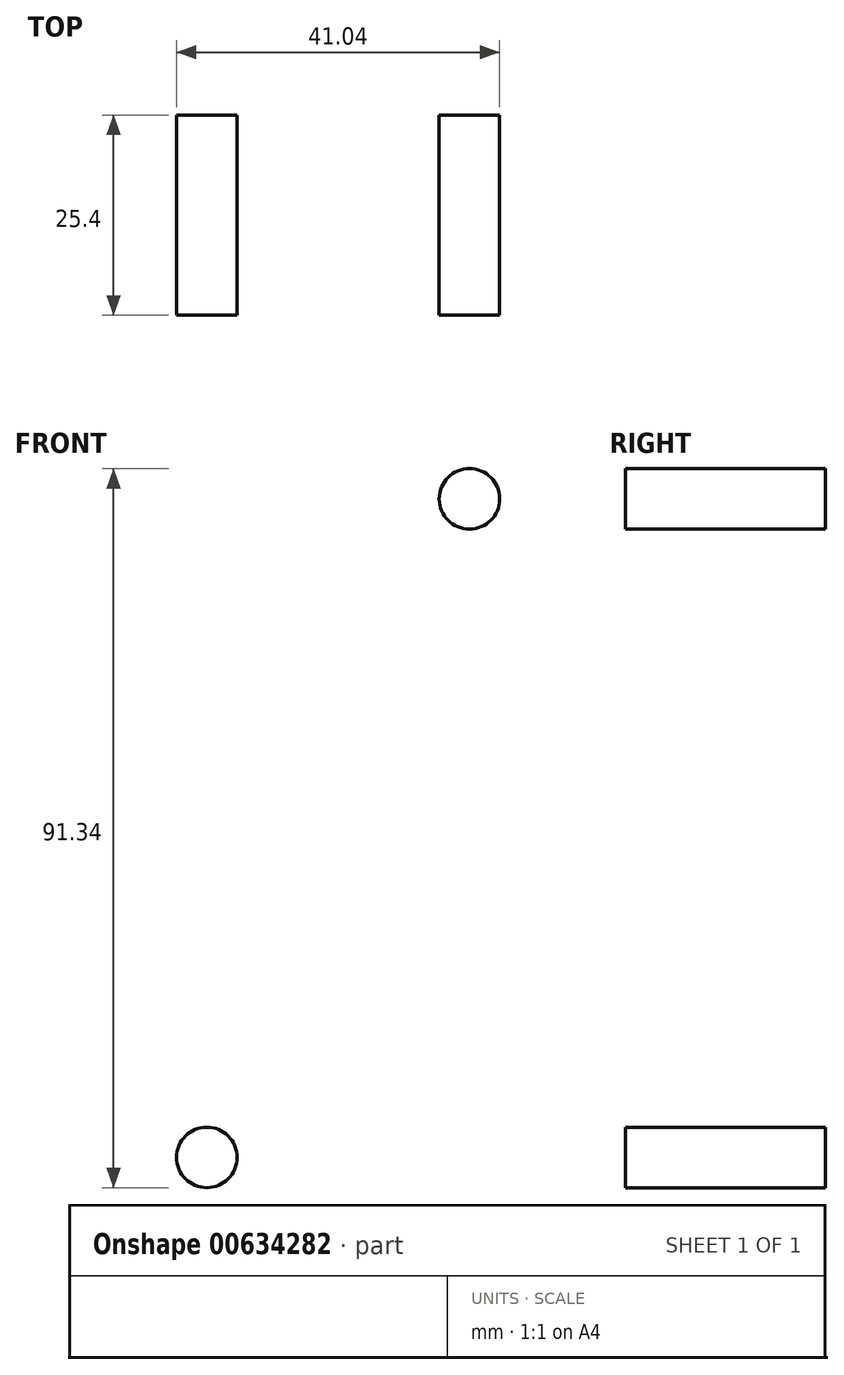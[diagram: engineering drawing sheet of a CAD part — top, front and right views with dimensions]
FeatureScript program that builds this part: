
annotation { "Feature Type Name" : "Feature", "Feature Type Description" : "" }
export const myFeature = defineFeature(function(context is Context, id is Id, definition is map)
    precondition{}
    {
        {
            var Q0;
            Q0=qCreatedBy(makeId("Front.planeOp"),FACE);
            var sketch = newSketch(context, id + "F0", { "sketchPlane" : qUnion([Q0])});
            skLineSegment(sketch, "E0.bottom", {"start": v(25.4, -50.8) * mm, "end": v(-25.4, -50.8) * mm});
            skLineSegment(sketch, "E0.top", {"start": v(25.4, 50.8) * mm, "end": v(-25.4, 50.8) * mm});
            skLineSegment(sketch, "E0.left", {"start": v(25.4, -50.8) * mm, "end": v(25.4, 50.8) * mm});
            skLineSegment(sketch, "E0.right", {"start": v(-25.4, -50.8) * mm, "end": v(-25.4, 50.8) * mm});
            skPoint(sketch, "E0.middle", {"position": v(0, 0) * mm});
            skCircle(sketch, "E1", {"center": v(0, -27.91) * mm, "radius": 7.62 * mm});
            skCircle(sketch, "E2.MirrorC", {"center": v(0, 27.91) * mm, "radius": 7.62 * mm});
            skSolve(sketch);
        }
        {
            var Q0;
            Q0=makeQuery(id+"F0.imprint","IMPRINT",FACE,{"disambiguationData":[TD([[makeQuery(id+"F0.imprint","IMPRINT",EDGE,{"derivedFrom":sQuery(id+"F0.wireOp",EDGE,"E0.bottom")}),-1.0]])]});
            extrude(context, id + "F1", {"entities" : qUnion([Q0]), "endBound" : BoundingType.SYMMETRIC, "depth" : 25.4 * mm, "offsetDistance" : 25.4 * mm});
        }
        {
            var Q0;
            Q0=makeQuery(id+"F1.opExtrude","SWEPT_EDGE",EDGE,{"disambiguationData":[OSD([sQuery(id+"F0.wireOp",EDGE,"E0.top"),sQuery(id+"F0.wireOp",EDGE,"E0.left")])]});
            var Q1;
            Q1=makeQuery(id+"F1.opExtrude","SWEPT_EDGE",EDGE,{"disambiguationData":[OSD([sQuery(id+"F0.wireOp",EDGE,"E0.bottom"),sQuery(id+"F0.wireOp",EDGE,"E0.left")])]});
            var Q2;
            Q2=makeQuery(id+"F1.opExtrude","SWEPT_EDGE",EDGE,{"disambiguationData":[OSD([sQuery(id+"F0.wireOp",EDGE,"E0.bottom"),sQuery(id+"F0.wireOp",EDGE,"E0.right")])]});
            var Q3;
            Q3=makeQuery(id+"F1.opExtrude","SWEPT_EDGE",EDGE,{"disambiguationData":[OSD([sQuery(id+"F0.wireOp",EDGE,"E0.top"),sQuery(id+"F0.wireOp",EDGE,"E0.right")])]});
            fillet(context, id + "F2", {"entities" : qUnion([Q0, Q1, Q2, Q3]), "radius" : 5.08 * mm, "tangentPropagation" : true, "allowEdgeOverflow" : false});
        }
        {
            var Q0;
            Q0=makeQuery(id+"F1.opExtrude","CAP_FACE",FACE,{"disambiguationData":[OSD([sQuery(id+"F0.wireOp",EDGE,"E0.bottom"),sQuery(id+"F0.wireOp",EDGE,"E0.top"),sQuery(id+"F0.wireOp",EDGE,"E0.left"),sQuery(id+"F0.wireOp",EDGE,"E0.right"),sQuery(id+"F0.wireOp",EDGE,"E1"),sQuery(id+"F0.wireOp",EDGE,"E2.MirrorC")])],"isStart":false});
            var sketch = newSketch(context, id + "F3", { "sketchPlane" : qUnion([Q0])});
            skCircle(sketch, "E3", {"center": v(-16.68, 41.83) * mm, "radius": 3.84 * mm});
            skCircle(sketch, "E4.MirrorC", {"center": v(16.68, 41.83) * mm, "radius": 3.84 * mm});
            skCircle(sketch, "E5.MirrorC", {"center": v(-16.68, -41.83) * mm, "radius": 3.84 * mm});
            skCircle(sketch, "E6.MirrorC", {"center": v(16.68, -41.83) * mm, "radius": 3.84 * mm});
            skSolve(sketch);
        }
        {
            var Q0;
            Q0=makeQuery(id+"F3.imprint","IMPRINT",FACE,{"disambiguationData":[TD([[makeQuery(id+"F3.imprint","IMPRINT",EDGE,{"derivedFrom":sQuery(id+"F3.wireOp",EDGE,"E3")}),1.0]])]});
            var Q1;
            Q1=makeQuery(id+"F3.imprint","IMPRINT",FACE,{"disambiguationData":[TD([[makeQuery(id+"F3.imprint","IMPRINT",EDGE,{"derivedFrom":sQuery(id+"F3.wireOp",EDGE,"E4.MirrorC")}),-1.0]])]});
            var Q2;
            Q2=makeQuery(id+"F3.imprint","IMPRINT",FACE,{"disambiguationData":[TD([[makeQuery(id+"F3.imprint","IMPRINT",EDGE,{"derivedFrom":sQuery(id+"F3.wireOp",EDGE,"E5.MirrorC")}),-1.0]])]});
            var Q3;
            Q3=makeQuery(id+"F3.imprint","IMPRINT",FACE,{"disambiguationData":[TD([[makeQuery(id+"F3.imprint","IMPRINT",EDGE,{"derivedFrom":sQuery(id+"F3.wireOp",EDGE,"E6.MirrorC")}),1.0]])]});
            var Q4;
            Q4=sQuery(id+"F3.wireOp",EDGE,"E3");
            var Q5;
            Q5=sQuery(id+"F3.wireOp",EDGE,"E4.MirrorC");
            var Q6;
            Q6=sQuery(id+"F3.wireOp",EDGE,"E5.MirrorC");
            var Q7;
            Q7=sQuery(id+"F3.wireOp",EDGE,"E6.MirrorC");
            extrude(context, id + "F4", {"entities" : qUnion([Q0, Q1, Q2, Q3]), "operationType" : NewBodyOperationType.REMOVE, "surfaceEntities" : qUnion([Q4, Q5, Q6, Q7]), "oppositeDirection" : true, "depth" : 25.4 * mm, "offsetDistance" : 25.4 * mm});
        }
    });
